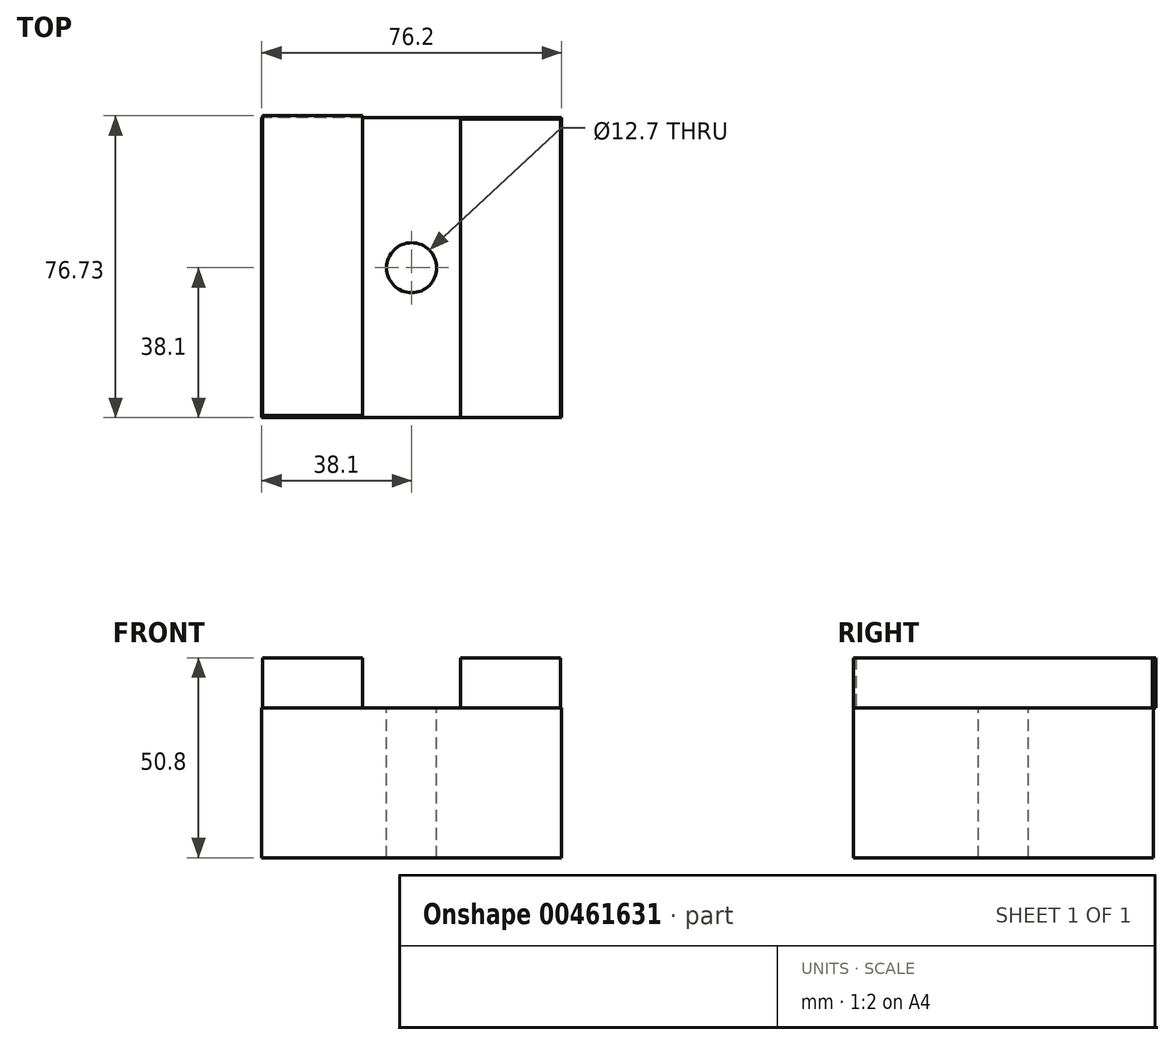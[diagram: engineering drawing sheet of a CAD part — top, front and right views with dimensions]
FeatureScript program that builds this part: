
annotation { "Feature Type Name" : "Feature", "Feature Type Description" : "" }
export const myFeature = defineFeature(function(context is Context, id is Id, definition is map)
    precondition{}
    {
        {
            var Q0;
            Q0=qCreatedBy(makeId("Top.planeOp"),FACE);
            var sketch = newSketch(context, id + "F0", { "sketchPlane" : qUnion([Q0])});
            skLineSegment(sketch, "E0.bottom", {"start": v(38.1, 38.1) * mm, "end": v(-38.1, 38.1) * mm});
            skLineSegment(sketch, "E0.top", {"start": v(38.1, -38.1) * mm, "end": v(-38.1, -38.1) * mm});
            skLineSegment(sketch, "E0.left", {"start": v(38.1, 38.1) * mm, "end": v(38.1, -38.1) * mm});
            skLineSegment(sketch, "E0.right", {"start": v(-38.1, 38.1) * mm, "end": v(-38.1, -38.1) * mm});
            skPoint(sketch, "E0.middle", {"position": v(0, 0) * mm});
            skSolve(sketch);
        }
        {
            var Q0;
            Q0=makeQuery(id+"F0.imprint","IMPRINT",FACE,{"disambiguationData":[TD([[makeQuery(id+"F0.imprint","IMPRINT",EDGE,{"derivedFrom":sQuery(id+"F0.wireOp",EDGE,"E0.bottom")}),1.0]])]});
            var sketch = newSketch(context, id + "F1", { "sketchPlane" : qUnion([Q0])});
            skLineSegment(sketch, "E1.bottom", {"start": v(-37.45, -37.2) * mm, "end": v(-12.05, -37.2) * mm});
            skLineSegment(sketch, "E1.top", {"start": v(-37.45, 39) * mm, "end": v(-12.05, 39) * mm});
            skLineSegment(sketch, "E1.left", {"start": v(-37.45, -37.2) * mm, "end": v(-37.45, 39) * mm});
            skLineSegment(sketch, "E1.right", {"start": v(-12.05, -37.2) * mm, "end": v(-12.05, 39) * mm});
            skLineSegment(sketch, "E2.bottom", {"start": v(37.88, -38.46) * mm, "end": v(12.48, -38.46) * mm});
            skLineSegment(sketch, "E2.top", {"start": v(37.88, 37.84) * mm, "end": v(12.48, 37.84) * mm});
            skLineSegment(sketch, "E2.left", {"start": v(37.88, -38.46) * mm, "end": v(37.88, 37.84) * mm});
            skLineSegment(sketch, "E2.right", {"start": v(12.48, -38.46) * mm, "end": v(12.48, 37.84) * mm});
            skSolve(sketch);
        }
        {
            var Q0;
            {var subQ0=sQuery(id+"F1.wireOp",EDGE,"E2.top");Q0=makeQuery(id+"F1.imprint","IMPRINT",FACE,{"disambiguationData":[TD([[makeQuery(id+"F1.imprint","IMPRINT",EDGE,{"derivedFrom":subQ0}),1.0]])]});}
            extrude(context, id + "F2", {"entities" : qUnion([Q0]), "depth" : 12.7 * mm});
        }
        {
            var Q0;
            Q0=makeQuery(id+"F0.imprint","IMPRINT",FACE,{"disambiguationData":[TD([[makeQuery(id+"F0.imprint","IMPRINT",EDGE,{"derivedFrom":sQuery(id+"F0.wireOp",EDGE,"E0.bottom")}),1.0]])]});
            var sketch = newSketch(context, id + "F3", { "sketchPlane" : qUnion([Q0])});
            skLineSegment(sketch, "E3.bottom", {"start": v(-37.87, -37.57) * mm, "end": v(-12.47, -37.57) * mm});
            skLineSegment(sketch, "E3.top", {"start": v(-37.87, 38.63) * mm, "end": v(-12.47, 38.63) * mm});
            skLineSegment(sketch, "E3.left", {"start": v(-37.87, -37.57) * mm, "end": v(-37.87, 38.63) * mm});
            skLineSegment(sketch, "E3.right", {"start": v(-12.47, -37.57) * mm, "end": v(-12.47, 38.63) * mm});
            skSolve(sketch);
        }
        {
            var Q0;
            Q0 = qSketchRegion(id + "F3", true);
            extrude(context, id + "F4", {"entities" : qUnion([Q0]), "depth" : 12.7 * mm});
        }
        {
            var Q0;
            Q0=makeQuery(id+"F0.imprint","IMPRINT",FACE,{"disambiguationData":[TD([[makeQuery(id+"F0.imprint","IMPRINT",EDGE,{"derivedFrom":sQuery(id+"F0.wireOp",EDGE,"E0.bottom")}),1.0]])]});
            extrude(context, id + "F5", {"entities" : qUnion([Q0]), "oppositeDirection" : true, "depth" : 38.1 * mm});
        }
        {
            var Q0;
            Q0=makeQuery(id+"F5.opExtrude","CAP_FACE",FACE,{"disambiguationData":[OSD([sQuery(id+"F0.wireOp",EDGE,"E0.bottom"),sQuery(id+"F0.wireOp",EDGE,"E0.top"),sQuery(id+"F0.wireOp",EDGE,"E0.left"),sQuery(id+"F0.wireOp",EDGE,"E0.right")])],"isStart":true});
            var sketch = newSketch(context, id + "F6", { "sketchPlane" : qUnion([Q0])});
            skPoint(sketch, "E4", {"position": v(0, 0) * mm});
            skLineSegment(sketch, "E5", {"start": v(-12.7, 38.1) * mm, "end": v(0, 38.1) * mm});
            skLineSegment(sketch, "E6", {"start": v(0, 38.1) * mm, "end": v(0, 0) * mm});
            skSolve(sketch);
        }
        {
            var Q0;
            Q0=sQuery(id+"F6.wireOp",VERTEX,"E4");
            var Q1;
            Q1=makeQuery(id+"F5.opExtrude","SWEPT_BODY",BODY,{"disambiguationData":[OSD([sQuery(id+"F0.wireOp",EDGE,"E0.bottom"),sQuery(id+"F0.wireOp",EDGE,"E0.top"),sQuery(id+"F0.wireOp",EDGE,"E0.left"),sQuery(id+"F0.wireOp",EDGE,"E0.right")])]});
            hole(context, id + "F7", {"style" : HoleStyle.SIMPLE, "endStyle" : HoleEndStyle.THROUGH, "holeDiameter" : 12.7 * mm, "isTappedThrough" : true, "tappedDepth" : 12.7 * mm, "tapClearance" : 3, "locations" : qUnion([Q0]), "scope" : qUnion([Q1])});
        }
    });
